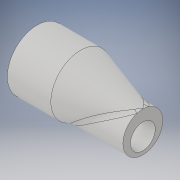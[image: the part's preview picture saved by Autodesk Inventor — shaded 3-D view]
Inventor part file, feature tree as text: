
AUTODESK INVENTOR PART (.ipt)
format: ipt  version: 2019 (Build 230136000, 136)  size: 550,912 bytes
history: native  units: in
note: dims shown in document units (in); Inventor stores cm internally (conversion verified against a paired STEP export)
features: sketch x14, extrude x7, revolve x4, fillet x4, plane x2, loft x1, other x1, projected_geometry x1
ambient origin geometry x8: Origin, YZ Plane, XZ Plane, XY Plane, X Axis, Y Axis, Z Axis, Center Point
bodies: Solid1 (feature_tree)
feature tree (34):
  revolve  "Revolution1"  Angle=90.0deg
  sketch  "Sketch2"  dims[d3=0.7874in d4=90.0deg]
  extrude  "Extrusion1"  Depth=0.5118in
  sketch  "Sketch4"  dims[d7=0.3937in d8=0.0in d9=0.7874in d10=0.0in d11=90.0deg]
  sketch  "Sketch5"  dims[d12=0.0in d13=90.0deg d14=0.2362in]
  loft  "Loft1"
  fillet  "Fillet1"  [1 undecoded]
  sketch  "Sketch6"  dims[d15=0.5118in d16=0.1969in d17=0.0in]
  plane  "Work Plane1"
  extrude  "Extrusion2"  Depth=0.2362in
  plane  "Work Plane2"
  extrude  "Extrusion4"  Depth=0.1969in TaperAngle=0.0deg
  sketch  "Sketch10"  dims[d29=0.1199in d30=1.1811in d31=0.0in]
  extrude  "Extrusion5"  Depth=0.7177in
  extrude  "Extrusion6"  Depth=0.3937in
  revolve  "Revolution2"  [1 undecoded]
  revolve  "Revolution3"  [1 undecoded]
  revolve  "Revolution4"  [1 undecoded]
  fillet  "Fillet2"  Radius=1.5804in
  extrude  "Extrusion8"  Depth=1.1149in
  fillet  "Fillet3"  Radius=1.1149in
  fillet  "Fillet4"  Radius=0.5497in
  extrude  "Extrusion9"  Depth=0.8268in
  sketch  "Sketch3"  dims[d5=0.0591in d6=0.5118in]
  other  "Edges1"
  sketch  "Sketch7"  dims[d18=0.6299in d19=0.7177in]
  sketch  "Sketch9"  dims[d26=1.2598in d28=0.3937in]
  sketch  "Sketch11"  dims[d32=1.2598in d33=1.8898in]
  sketch  "Sketch13"  dims[d34=0.3937in d35=0.0in d36=0.1969in d37=0.0in d38=1.5804in]
  projected_geometry  "Projected Loop1"
  sketch  "Sketch14"  dims[d39=0.9449in d41=1.1149in d42=1.1149in d43=0.5497in]
  sketch  "Sketch15"  dims[d44=0.8268in d45=1.924in]
  sketch  "Sketch17"  dims[d46=0.3937in]
  sketch  "Sketch18"  dims[d51=0.4724in d52=0.0in d53=0.0787in d54=0.0787in d56=1.1811in d57=0.0in]
note: 4 required parameter values undecoded (feature->parameter linkage not recoverable at this tier; creation-order binding heuristic only, values carry confidence <= 0.55)